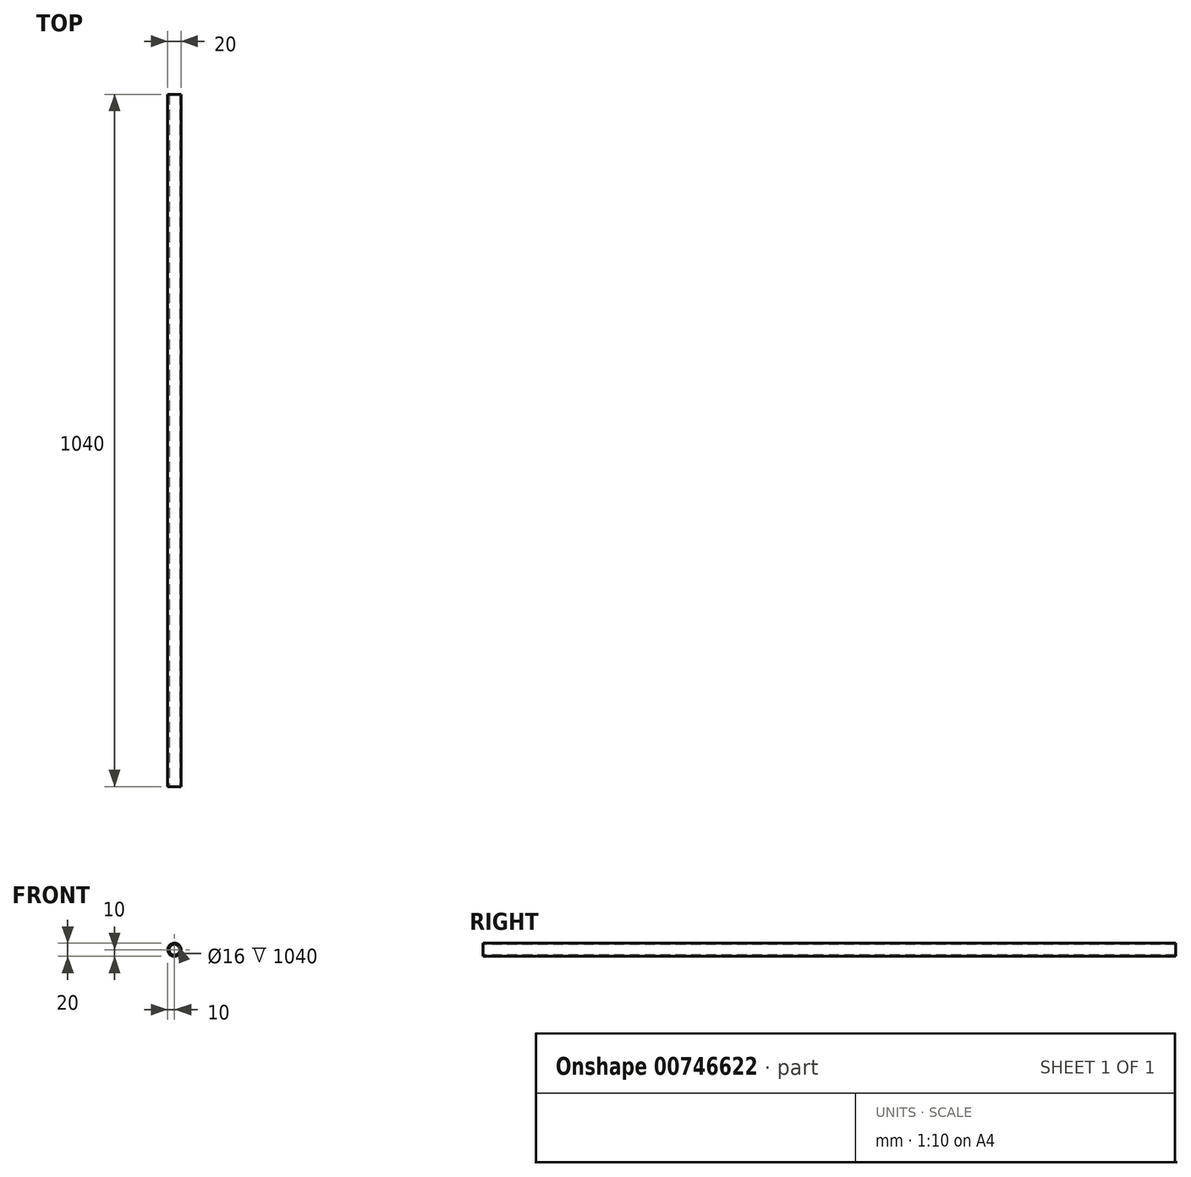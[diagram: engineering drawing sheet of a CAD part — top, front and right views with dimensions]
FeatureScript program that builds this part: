
annotation { "Feature Type Name" : "Feature", "Feature Type Description" : "" }
export const myFeature = defineFeature(function(context is Context, id is Id, definition is map)
    precondition{}
    {
        {
            var Q0;
            Q0=qCreatedBy(makeId("Front.planeOp"),FACE);
            var sketch = newSketch(context, id + "F0", { "sketchPlane" : qUnion([Q0])});
            skCircle(sketch, "E0", {"center": v(0, 0) * mm, "radius": 10 * mm});
            skCircle(sketch, "E1", {"center": v(0, 0) * mm, "radius": 8 * mm});
            skSolve(sketch);
        }
        {
            var Q0;
            Q0 = qSketchRegion(id + "F0", true);
            var Q1;
            Q1=makeQuery(id+"F0.imprint","IMPRINT",FACE,{"disambiguationData":[TD([[makeQuery(id+"F0.imprint","IMPRINT",EDGE,{"derivedFrom":sQuery(id+"F0.wireOp",EDGE,"E0")}),1.0]])]});
            extrude(context, id + "F1", {"entities" : qUnion([Q0, Q1]), "oppositeDirection" : true, "depth" : 1040 * mm, "offsetDistance" : 25 * mm});
        }
    });
